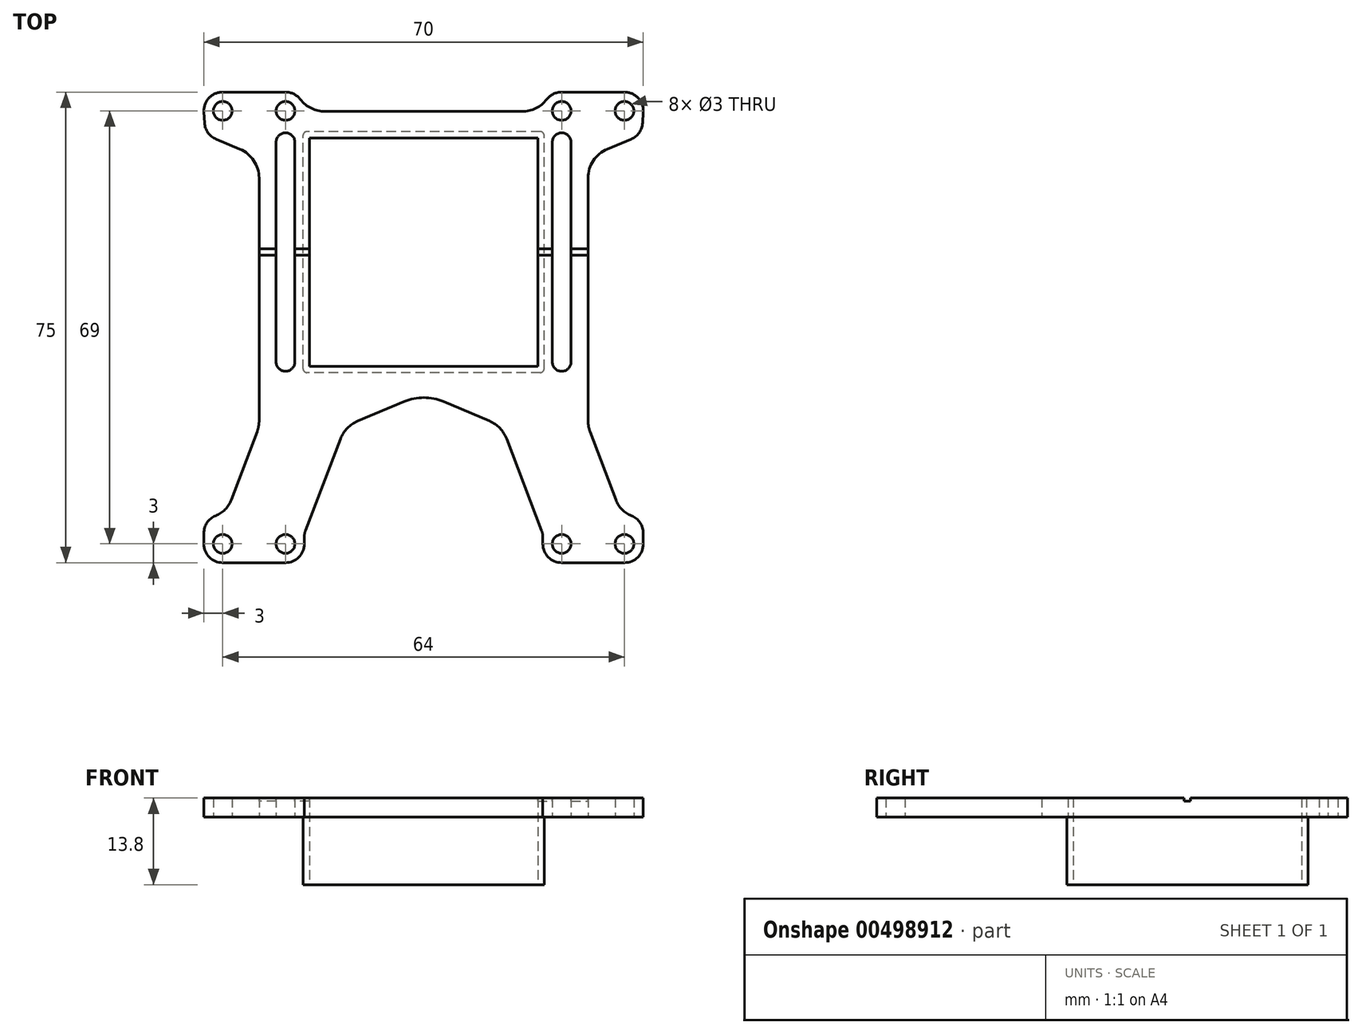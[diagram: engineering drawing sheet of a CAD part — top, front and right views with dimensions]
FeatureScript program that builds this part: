
annotation { "Feature Type Name" : "Feature", "Feature Type Description" : "" }
export const myFeature = defineFeature(function(context is Context, id is Id, definition is map)
    precondition{}
    {
        {
            var Q0;
            Q0=qCreatedBy(makeId("Top.planeOp"),FACE);
            var sketch = newSketch(context, id + "F0", { "sketchPlane" : qUnion([Q0])});
            skLineSegment(sketch, "E0.bottom", {"start": v(-1.83, 2.38) * mm, "end": v(1.83, 2.38) * mm, "construction": true});
            skLineSegment(sketch, "E0.top", {"start": v(-1.83, -2.37) * mm, "end": v(1.83, -2.37) * mm, "construction": true});
            skLineSegment(sketch, "E0.left", {"start": v(-1.83, 2.38) * mm, "end": v(-1.83, -2.37) * mm, "construction": true});
            skLineSegment(sketch, "E0.right", {"start": v(1.83, 2.38) * mm, "end": v(1.83, -2.37) * mm, "construction": true});
            skLineSegment(sketch, "E1.bottom", {"start": v(-1.28, 1.65) * mm, "end": v(1.32, 1.65) * mm, "construction": true});
            skLineSegment(sketch, "E1.top", {"start": v(-1.28, -0.31) * mm, "end": v(1.32, -0.31) * mm, "construction": true});
            skLineSegment(sketch, "E1.left", {"start": v(-1.28, 1.65) * mm, "end": v(-1.28, -0.31) * mm, "construction": true});
            skLineSegment(sketch, "E1.right", {"start": v(1.32, 1.65) * mm, "end": v(1.32, -0.31) * mm, "construction": true});
            skLineSegment(sketch, "E2", {"start": v(-1.28, 1.65) * mm, "end": v(1.32, -0.31) * mm, "construction": true});
            skLineSegment(sketch, "E3", {"start": v(1.32, 1.65) * mm, "end": v(-1.28, -0.31) * mm, "construction": true});
            skPoint(sketch, "E4", {"position": v(0.02, 0.67) * mm});
            skLineSegment(sketch, "E5.bottom", {"start": v(35, -49.5) * mm, "end": v(-35, -49.5) * mm, "construction": true});
            skLineSegment(sketch, "E5.top", {"start": v(35, 40.5) * mm, "end": v(-35, 40.5) * mm, "construction": true});
            skLineSegment(sketch, "E5.left", {"start": v(35, -49.5) * mm, "end": v(35, 40.5) * mm, "construction": true});
            skLineSegment(sketch, "E5.right", {"start": v(-35, -49.5) * mm, "end": v(-35, 40.5) * mm, "construction": true});
            skPoint(sketch, "E5.middle", {"position": v(0, 0) * mm});
            skLineSegment(sketch, "E6.bottom", {"start": v(18, -18) * mm, "end": v(-18, -18) * mm, "construction": true});
            skLineSegment(sketch, "E6.top", {"start": v(18, 18) * mm, "end": v(-18, 18) * mm, "construction": true});
            skLineSegment(sketch, "E6.left", {"start": v(18, -18) * mm, "end": v(18, 18) * mm, "construction": true});
            skLineSegment(sketch, "E6.right", {"start": v(-18, -18) * mm, "end": v(-18, 18) * mm, "construction": true});
            skPoint(sketch, "E7", {"position": v(-32, -46.5) * mm});
            skPoint(sketch, "E8", {"position": v(-22, -46.5) * mm});
            skPoint(sketch, "E9", {"position": v(22, -46.5) * mm});
            skPoint(sketch, "E10", {"position": v(32, -46.5) * mm});
            skPoint(sketch, "E11", {"position": v(32, 22.5) * mm});
            skPoint(sketch, "E12", {"position": v(22, 22.5) * mm});
            skPoint(sketch, "E12.positionSnap0", {"position": v(18, 0) * mm});
            skPoint(sketch, "E13", {"position": v(-22, 22.5) * mm});
            skPoint(sketch, "E14", {"position": v(-32, 22.5) * mm});
            skCircle(sketch, "E15", {"center": v(-32, 22.5) * mm, "radius": 1.25 * mm, "construction": true});
            skCircle(sketch, "E16", {"center": v(-22, 22.5) * mm, "radius": 1.25 * mm, "construction": true});
            skCircle(sketch, "E17", {"center": v(22, 22.5) * mm, "radius": 1.25 * mm, "construction": true});
            skCircle(sketch, "E18", {"center": v(32, 22.5) * mm, "radius": 1.25 * mm, "construction": true});
            skCircle(sketch, "E19", {"center": v(-32, -46.5) * mm, "radius": 1.25 * mm, "construction": true});
            skCircle(sketch, "E20", {"center": v(22, -46.5) * mm, "radius": 1.25 * mm, "construction": true});
            skCircle(sketch, "E21", {"center": v(32, -46.5) * mm, "radius": 1.25 * mm, "construction": true});
            skCircle(sketch, "E22", {"center": v(-22, -46.5) * mm, "radius": 1.25 * mm, "construction": true});
            skLineSegment(sketch, "E23.bottom", {"start": v(15, -15) * mm, "end": v(-15, -15) * mm, "construction": true});
            skLineSegment(sketch, "E23.top", {"start": v(15, 15) * mm, "end": v(-15, 15) * mm, "construction": true});
            skLineSegment(sketch, "E23.left", {"start": v(15, -15) * mm, "end": v(15, 15) * mm, "construction": true});
            skLineSegment(sketch, "E23.right", {"start": v(-15, -15) * mm, "end": v(-15, 15) * mm, "construction": true});
            skLineSegment(sketch, "E24.bottom", {"start": v(9.5, -9.5) * mm, "end": v(-9.5, -9.5) * mm, "construction": true});
            skLineSegment(sketch, "E24.top", {"start": v(9.5, 9.5) * mm, "end": v(-9.5, 9.5) * mm, "construction": true});
            skLineSegment(sketch, "E24.left", {"start": v(9.5, -9.5) * mm, "end": v(9.5, 9.5) * mm, "construction": true});
            skLineSegment(sketch, "E24.right", {"start": v(-9.5, -9.5) * mm, "end": v(-9.5, 9.5) * mm, "construction": true});
            skSolve(sketch);
        }
        {
            var Q0;
            Q0=qCreatedBy(makeId("Top.planeOp"),FACE);
            var sketch = newSketch(context, id + "F1", { "sketchPlane" : qUnion([Q0])});
            skLineSegment(sketch, "E25.bottom", {"start": v(18.2, -18.2) * mm, "end": v(-18.2, -18.2) * mm});
            skLineSegment(sketch, "E25.top", {"start": v(18.2, 18.2) * mm, "end": v(-18.2, 18.2) * mm});
            skLineSegment(sketch, "E25.left", {"start": v(18.2, -18.2) * mm, "end": v(18.2, 18.2) * mm});
            skLineSegment(sketch, "E25.right", {"start": v(-18.2, -18.2) * mm, "end": v(-18.2, 18.2) * mm});
            skPoint(sketch, "E25.middle", {"position": v(0, 0) * mm});
            skLineSegment(sketch, "E26.bottom", {"start": v(19.2, -19.2) * mm, "end": v(-19.2, -19.2) * mm});
            skLineSegment(sketch, "E26.top", {"start": v(19.2, 19.2) * mm, "end": v(-19.2, 19.2) * mm});
            skLineSegment(sketch, "E26.left", {"start": v(19.2, -19.2) * mm, "end": v(19.2, 19.2) * mm});
            skLineSegment(sketch, "E26.right", {"start": v(-19.2, -19.2) * mm, "end": v(-19.2, 19.2) * mm});
            skSolve(sketch);
        }
        {
            var Q0;
            Q0=makeQuery(id+"F1.imprint","IMPRINT",FACE,{"disambiguationData":[TD([[makeQuery(id+"F1.imprint","IMPRINT",EDGE,{"derivedFrom":sQuery(id+"F1.wireOp",EDGE,"E25.bottom")}),1.0]])]});
            extrude(context, id + "F2", {"entities" : qUnion([Q0]), "depth" : (4.8 + 7) * mm, "offsetDistance" : 25 * mm});
        }
        {
            var Q0;
            Q0=makeQuery(id+"F2.opExtrude","CAP_FACE",FACE,{"disambiguationData":[OSD([sQuery(id+"F1.wireOp",EDGE,"E25.bottom"),sQuery(id+"F1.wireOp",EDGE,"E25.top"),sQuery(id+"F1.wireOp",EDGE,"E25.left"),sQuery(id+"F1.wireOp",EDGE,"E25.right"),sQuery(id+"F1.wireOp",EDGE,"E26.bottom"),sQuery(id+"F1.wireOp",EDGE,"E26.top"),sQuery(id+"F1.wireOp",EDGE,"E26.left"),sQuery(id+"F1.wireOp",EDGE,"E26.right")])],"isStart":false});
            var sketch = newSketch(context, id + "F3", { "sketchPlane" : qUnion([Q0])});
            skPoint(sketch, "E27.0", {"position": v(-35, -49.5) * mm});
            skPoint(sketch, "E28.0", {"position": v(35, -49.5) * mm});
            skLineSegment(sketch, "E29", {"start": v(-35, 25.5) * mm, "end": v(35, 25.5) * mm, "construction": true});
            skLineSegment(sketch, "E30.bottom", {"start": v(-32, -49.5) * mm, "end": v(-22, -49.5) * mm});
            skLineSegment(sketch, "E30.left", {"start": v(-35, -46.5) * mm, "end": v(-35, -44.8) * mm});
            skLineSegment(sketch, "E30.right", {"start": v(-19, -46.5) * mm, "end": v(-19, -45.44) * mm});
            skLineSegment(sketch, "E31.bottom", {"start": v(32, -49.5) * mm, "end": v(22, -49.5) * mm});
            skLineSegment(sketch, "E31.left", {"start": v(35, -46.5) * mm, "end": v(35, -44.8) * mm});
            skLineSegment(sketch, "E31.right", {"start": v(19, -46.5) * mm, "end": v(19, -45.44) * mm});
            skPoint(sketch, "E32.0", {"position": v(-19.2, -19.2) * mm});
            skPoint(sketch, "E33.0", {"position": v(19.2, -19.2) * mm});
            skArc(sketch, "E34", {"start": v(-30.65, -39.5) * mm, "mid": v(-31.62, -41.02) * mm, "end": v(-33.12, -42.02) * mm});
            skLineSegment(sketch, "E35", {"start": v(-18.8, -44.37) * mm, "end": v(-13.23, -29.76) * mm});
            skArc(sketch, "E36.MirrorCS", {"start": v(30.65, -39.5) * mm, "mid": v(31.62, -41.02) * mm, "end": v(33.12, -42.02) * mm});
            skLineSegment(sketch, "E37.MirrorCS", {"start": v(18.8, -44.37) * mm, "end": v(13.23, -29.76) * mm});
            skPoint(sketch, "E38.orphan", {"position": v(19, -39.5) * mm});
            skPoint(sketch, "E39.orphan", {"position": v(-19, -39.5) * mm});
            skPoint(sketch, "E40.visualSharp", {"position": v(-35, -42.32) * mm});
            skArc(sketch, "E40.filletArc", {"start": v(-33.12, -42.02) * mm, "mid": v(-34.48, -43.12) * mm, "end": v(-35, -44.8) * mm});
            skPoint(sketch, "E41.visualSharp", {"position": v(35, -42.32) * mm});
            skArc(sketch, "E41.filletArc", {"start": v(35, -44.8) * mm, "mid": v(34.48, -43.12) * mm, "end": v(33.12, -42.02) * mm});
            skArc(sketch, "E42.filletArc", {"start": v(32, -49.5) * mm, "mid": v(34.12, -48.62) * mm, "end": v(35, -46.5) * mm});
            skPoint(sketch, "E43.visualSharp", {"position": v(19, -49.5) * mm});
            skArc(sketch, "E43.filletArc", {"start": v(19, -46.5) * mm, "mid": v(19.88, -48.62) * mm, "end": v(22, -49.5) * mm});
            skPoint(sketch, "E44.visualSharp", {"position": v(-19, -49.5) * mm});
            skArc(sketch, "E44.filletArc", {"start": v(-22, -49.5) * mm, "mid": v(-19.88, -48.62) * mm, "end": v(-19, -46.5) * mm});
            skArc(sketch, "E45.filletArc", {"start": v(-35, -46.5) * mm, "mid": v(-34.12, -48.62) * mm, "end": v(-32, -49.5) * mm});
            skPoint(sketch, "E46.visualSharp", {"position": v(-19, -44.89) * mm});
            skArc(sketch, "E46.filletArc", {"start": v(-18.8, -44.37) * mm, "mid": v(-18.95, -44.9) * mm, "end": v(-19, -45.44) * mm});
            skPoint(sketch, "E47.visualSharp", {"position": v(19, -44.89) * mm});
            skArc(sketch, "E47.filletArc", {"start": v(19, -45.44) * mm, "mid": v(18.95, -44.9) * mm, "end": v(18.8, -44.37) * mm});
            skPoint(sketch, "E48.0", {"position": v(-32, 22.5) * mm});
            skPoint(sketch, "E49.0", {"position": v(-22, 22.5) * mm});
            skPoint(sketch, "E50.0", {"position": v(22, 22.5) * mm});
            skPoint(sketch, "E51.0", {"position": v(32, 22.5) * mm});
            skLineSegment(sketch, "E52.bottom", {"start": v(-32, 25.5) * mm, "end": v(-22, 25.5) * mm});
            skLineSegment(sketch, "E52.left", {"start": v(-35, 22.32) * mm, "end": v(-34.9, 20.58) * mm});
            skArc(sketch, "E53.filletArc", {"start": v(-34.9, 20.58) * mm, "mid": v(-34.34, 19.02) * mm, "end": v(-33.05, 18) * mm});
            skArc(sketch, "E54.filletArc", {"start": v(-32, 25.5) * mm, "mid": v(-34.18, 24.56) * mm, "end": v(-35, 22.32) * mm});
            skArc(sketch, "E55.filletArc", {"start": v(-19.63, 24.33) * mm, "mid": v(-20.68, 25.19) * mm, "end": v(-22, 25.5) * mm});
            skLineSegment(sketch, "E56", {"start": v(-33.05, 18) * mm, "end": v(-29.27, 16.41) * mm});
            skLineSegment(sketch, "E57.MirrorCS", {"start": v(35, 22.32) * mm, "end": v(34.9, 20.58) * mm});
            skArc(sketch, "E58.MirrorCS", {"start": v(19.63, 24.33) * mm, "mid": v(20.68, 25.19) * mm, "end": v(22, 25.5) * mm});
            skArc(sketch, "E59.MirrorCS", {"start": v(34.9, 20.58) * mm, "mid": v(34.34, 19.02) * mm, "end": v(33.05, 18) * mm});
            skArc(sketch, "E60.MirrorCS", {"start": v(32, 25.5) * mm, "mid": v(34.18, 24.56) * mm, "end": v(35, 22.32) * mm});
            skLineSegment(sketch, "E61.MirrorCS", {"start": v(32, 25.5) * mm, "end": v(22, 25.5) * mm});
            skLineSegment(sketch, "E62.MirrorCS", {"start": v(33.05, 18) * mm, "end": v(29.27, 16.41) * mm});
            skLineSegment(sketch, "E63", {"start": v(-15.68, 22.4) * mm, "end": v(15.68, 22.4) * mm});
            skLineSegment(sketch, "E64", {"start": v(-26.2, -26.85) * mm, "end": v(-26.2, 11.8) * mm});
            skLineSegment(sketch, "E65", {"start": v(-32, 22.5) * mm, "end": v(-22, 22.5) * mm, "construction": true});
            skCircle(sketch, "E66", {"center": v(-32, 22.5) * mm, "radius": 1.5 * mm});
            skCircle(sketch, "E67", {"center": v(32, 22.5) * mm, "radius": 1.5 * mm});
            skCircle(sketch, "E68", {"center": v(-32, -46.5) * mm, "radius": 1.5 * mm});
            skCircle(sketch, "E69", {"center": v(-22, -46.5) * mm, "radius": 1.5 * mm});
            skCircle(sketch, "E70", {"center": v(22, -46.5) * mm, "radius": 1.5 * mm});
            skCircle(sketch, "E71", {"center": v(32, -46.5) * mm, "radius": 1.5 * mm});
            skCircle(sketch, "E72", {"center": v(-22, 22.5) * mm, "radius": 1.5 * mm});
            skCircle(sketch, "E73", {"center": v(22, 22.5) * mm, "radius": 1.5 * mm});
            skCircle(sketch, "E74.0", {"center": v(-22, 0) * mm, "radius": 1.5 * mm, "construction": true});
            skCircle(sketch, "E75.0", {"center": v(-22, 10) * mm, "radius": 1.5 * mm, "construction": true});
            skCircle(sketch, "E76.0", {"center": v(-22, -10) * mm, "radius": 1.5 * mm, "construction": true});
            skArc(sketch, "E77.0.1.0", {"start": v(-23.5, -17.5) * mm, "mid": v(-22, -19) * mm, "end": v(-20.5, -17.5) * mm});
            skLineSegment(sketch, "E77.direction1", {"start": v(-22, -10) * mm, "end": v(3, -10) * mm, "construction": true});
            skLineSegment(sketch, "E77.direction2", {"start": v(-22, -10) * mm, "end": v(-22, -17.5) * mm, "construction": true});
            skArc(sketch, "E78.0.1.0", {"start": v(-20.5, 17.5) * mm, "mid": v(-22, 19) * mm, "end": v(-23.5, 17.5) * mm});
            skLineSegment(sketch, "E78.direction1", {"start": v(-22, 10) * mm, "end": v(3, 10) * mm, "construction": true});
            skLineSegment(sketch, "E78.direction2", {"start": v(-22, 10) * mm, "end": v(-22, 17.5) * mm, "construction": true});
            skLineSegment(sketch, "E79", {"start": v(-20.5, 17.5) * mm, "end": v(-20.5, -17.5) * mm});
            skLineSegment(sketch, "E80", {"start": v(-23.5, 17.5) * mm, "end": v(-23.5, -17.5) * mm});
            skArc(sketch, "E81.trimOffspring", {"start": v(-21.84, -16) * mm, "mid": v(-21.92, -16) * mm, "end": v(-22, -16) * mm});
            skLineSegment(sketch, "E82", {"start": v(-10.5, -26.94) * mm, "end": v(-3.06, -23.82) * mm});
            skLineSegment(sketch, "E83", {"start": v(3.15, -23.82) * mm, "end": v(10.5, -26.93) * mm});
            skPoint(sketch, "E84.orphan", {"position": v(-10.37, -22.5) * mm});
            skPoint(sketch, "E85.end.orphan", {"position": v(10.47, -22.53) * mm});
            skPoint(sketch, "E86.visualSharp", {"position": v(0.05, -22.51) * mm});
            skArc(sketch, "E86.filletArc", {"start": v(3.15, -23.82) * mm, "mid": v(0.05, -23.2) * mm, "end": v(-3.06, -23.82) * mm});
            skPoint(sketch, "E87.orphan", {"position": v(-26.2, 16.8) * mm});
            skPoint(sketch, "E88.trimOffspring.end.orphan", {"position": v(-19.2, 12.2) * mm});
            skLineSegment(sketch, "E89.trimOffspring", {"start": v(-26.52, -28.62) * mm, "end": v(-30.65, -39.5) * mm});
            skPoint(sketch, "E90.start.orphan", {"position": v(-19.2, -9.2) * mm});
            skPoint(sketch, "E91.trimOffspring.end.orphan", {"position": v(-9.2, -19.2) * mm});
            skPoint(sketch, "E92.orphan", {"position": v(9.2, -19.2) * mm});
            skLineSegment(sketch, "E93.MirrorCS", {"start": v(26.2, -26.85) * mm, "end": v(26.2, 11.8) * mm});
            skCircle(sketch, "E94.MirrorC", {"center": v(22, 10) * mm, "radius": 1.5 * mm, "construction": true});
            skLineSegment(sketch, "E95.MirrorCS", {"start": v(23.5, 17.5) * mm, "end": v(23.5, -17.5) * mm});
            skLineSegment(sketch, "E96.MirrorCS", {"start": v(22, -10) * mm, "end": v(22, -17.5) * mm, "construction": true});
            skLineSegment(sketch, "E97.MirrorCS", {"start": v(22, 10) * mm, "end": v(22, 17.5) * mm, "construction": true});
            skCircle(sketch, "E98.MirrorC", {"center": v(22, -10) * mm, "radius": 1.5 * mm, "construction": true});
            skArc(sketch, "E99.MirrorCS", {"start": v(20.5, 17.5) * mm, "mid": v(22, 19) * mm, "end": v(23.5, 17.5) * mm});
            skArc(sketch, "E100.MirrorCS", {"start": v(23.5, -17.5) * mm, "mid": v(22, -19) * mm, "end": v(20.5, -17.5) * mm});
            skLineSegment(sketch, "E101.MirrorCS", {"start": v(20.5, 17.5) * mm, "end": v(20.5, -17.5) * mm});
            skCircle(sketch, "E102.MirrorC", {"center": v(22, 0) * mm, "radius": 1.5 * mm, "construction": true});
            skLineSegment(sketch, "E103.trimOffspring", {"start": v(26.52, -28.62) * mm, "end": v(30.65, -39.5) * mm});
            skPoint(sketch, "E104.MirrorCS.end.orphan", {"position": v(22, -16) * mm});
            skPoint(sketch, "E104.MirrorCS.start.orphan", {"position": v(21.84, -16) * mm});
            skPoint(sketch, "E105.end.orphan", {"position": v(19.2, 12.2) * mm});
            skPoint(sketch, "E105.start.orphan", {"position": v(19.2, -9.2) * mm});
            skPoint(sketch, "E106.MirrorCS.end.orphan", {"position": v(19, 19.2) * mm});
            skPoint(sketch, "E107.MirrorCS.end.orphan", {"position": v(19, 21.46) * mm});
            skPoint(sketch, "E108.end.orphan", {"position": v(-19, 19.2) * mm});
            skPoint(sketch, "E52.right.end.orphan", {"position": v(-19, 21.46) * mm});
            skPoint(sketch, "E109.visualSharp", {"position": v(-26.2, -27.76) * mm});
            skArc(sketch, "E109.filletArc", {"start": v(-26.52, -28.62) * mm, "mid": v(-26.28, -27.75) * mm, "end": v(-26.2, -26.85) * mm});
            skPoint(sketch, "E110.visualSharp", {"position": v(26.2, -27.76) * mm});
            skArc(sketch, "E110.filletArc", {"start": v(26.2, -26.85) * mm, "mid": v(26.28, -27.75) * mm, "end": v(26.52, -28.62) * mm});
            skPoint(sketch, "E111.visualSharp", {"position": v(-12.47, -27.76) * mm});
            skArc(sketch, "E111.filletArc", {"start": v(-10.5, -26.94) * mm, "mid": v(-12.15, -28.07) * mm, "end": v(-13.23, -29.76) * mm});
            skPoint(sketch, "E112.visualSharp", {"position": v(12.47, -27.76) * mm});
            skArc(sketch, "E112.filletArc", {"start": v(13.23, -29.76) * mm, "mid": v(12.15, -28.07) * mm, "end": v(10.5, -26.93) * mm});
            skPoint(sketch, "E113.visualSharp", {"position": v(-19, 22.4) * mm});
            skArc(sketch, "E113.filletArc", {"start": v(-19.63, 24.33) * mm, "mid": v(-17.88, 22.9) * mm, "end": v(-15.68, 22.4) * mm});
            skPoint(sketch, "E114.visualSharp", {"position": v(19, 22.4) * mm});
            skArc(sketch, "E114.filletArc", {"start": v(15.68, 22.4) * mm, "mid": v(17.88, 22.9) * mm, "end": v(19.63, 24.33) * mm});
            skPoint(sketch, "E115.visualSharp", {"position": v(26.2, 15.13) * mm});
            skArc(sketch, "E115.filletArc", {"start": v(29.27, 16.41) * mm, "mid": v(27.04, 14.57) * mm, "end": v(26.2, 11.8) * mm});
            skPoint(sketch, "E116.visualSharp", {"position": v(-26.2, 15.13) * mm});
            skArc(sketch, "E116.filletArc", {"start": v(-26.2, 11.8) * mm, "mid": v(-27.04, 14.57) * mm, "end": v(-29.27, 16.41) * mm});
            skPoint(sketch, "E117.0", {"position": v(0, 0) * mm});
            skSolve(sketch);
        }
        {
            var Q0;
            Q0=makeQuery(id+"F3.imprint","IMPRINT",FACE,{"disambiguationData":[TD([[makeQuery(id+"F3.imprint","IMPRINT",EDGE,{"derivedFrom":sQuery(id+"F3.wireOp",EDGE,"E30.bottom")}),1.0]])]});
            var Q1;
            Q1=makeQuery(id+"F3.imprint","IMPRINT",FACE,{"disambiguationData":[TD([[makeQuery(id+"F3.imprint","IMPRINT",EDGE,{"derivedFrom":makeQuery(id+"F2.opExtrude","CAP_EDGE",EDGE,{"disambiguationData":[OSD([sQuery(id+"F1.wireOp",EDGE,"E25.bottom")])],"isStart":false})}),1.0]])]});
            extrude(context, id + "F4", {"entities" : qUnion([Q0, Q1]), "operationType" : NewBodyOperationType.ADD, "depth" : 2 * mm, "hasSecondDirection" : true, "secondDirectionOppositeDirection" : true, "secondDirectionDepth" : 1 * mm, "offsetDistance" : 25 * mm});
        }
        {
            var Q0;
            Q0=makeQuery(id+"F2.opExtrude","SWEPT_EDGE",EDGE,{"disambiguationData":[OSD([sQuery(id+"F1.wireOp",EDGE,"E26.bottom"),sQuery(id+"F1.wireOp",EDGE,"E26.right")])]});
            var Q1;
            Q1=makeQuery(id+"F2.opExtrude","SWEPT_EDGE",EDGE,{"disambiguationData":[OSD([sQuery(id+"F1.wireOp",EDGE,"E26.bottom"),sQuery(id+"F1.wireOp",EDGE,"E26.left")])]});
            var Q2;
            Q2=makeQuery(id+"F2.opExtrude","SWEPT_EDGE",EDGE,{"disambiguationData":[OSD([sQuery(id+"F1.wireOp",EDGE,"E26.top"),sQuery(id+"F1.wireOp",EDGE,"E26.left")])]});
            var Q3;
            Q3=makeQuery(id+"F2.opExtrude","SWEPT_EDGE",EDGE,{"disambiguationData":[OSD([sQuery(id+"F1.wireOp",EDGE,"E26.top"),sQuery(id+"F1.wireOp",EDGE,"E26.right")])]});
            fillet(context, id + "F5", {"entities" : qUnion([Q0, Q1, Q2, Q3]), "radius" : 0.6 * mm, "tangentPropagation" : true, "allowEdgeOverflow" : false});
        }
        {
            var Q0;
            Q0=makeQuery(id+"F4.opExtrude","CAP_FACE",FACE,{"disambiguationData":[OSD([sQuery(id+"F1.wireOp",EDGE,"E25.bottom"),sQuery(id+"F1.wireOp",EDGE,"E25.top"),sQuery(id+"F1.wireOp",EDGE,"E25.left"),sQuery(id+"F1.wireOp",EDGE,"E25.right"),sQuery(id+"F3.wireOp",EDGE,"E30.bottom"),sQuery(id+"F3.wireOp",EDGE,"E30.left"),sQuery(id+"F3.wireOp",EDGE,"E30.right"),sQuery(id+"F3.wireOp",EDGE,"E31.bottom"),sQuery(id+"F3.wireOp",EDGE,"E31.left"),sQuery(id+"F3.wireOp",EDGE,"E31.right"),sQuery(id+"F3.wireOp",EDGE,"E34"),sQuery(id+"F3.wireOp",EDGE,"E35"),sQuery(id+"F3.wireOp",EDGE,"E36.MirrorCS"),sQuery(id+"F3.wireOp",EDGE,"E37.MirrorCS"),sQuery(id+"F3.wireOp",EDGE,"E40.filletArc"),sQuery(id+"F3.wireOp",EDGE,"E41.filletArc"),sQuery(id+"F3.wireOp",EDGE,"E42.filletArc"),sQuery(id+"F3.wireOp",EDGE,"E43.filletArc"),sQuery(id+"F3.wireOp",EDGE,"E44.filletArc"),sQuery(id+"F3.wireOp",EDGE,"E45.filletArc"),sQuery(id+"F3.wireOp",EDGE,"E46.filletArc"),sQuery(id+"F3.wireOp",EDGE,"E47.filletArc"),sQuery(id+"F3.wireOp",EDGE,"E52.bottom"),sQuery(id+"F3.wireOp",EDGE,"E52.left"),sQuery(id+"F3.wireOp",EDGE,"E53.filletArc"),sQuery(id+"F3.wireOp",EDGE,"E54.filletArc"),sQuery(id+"F3.wireOp",EDGE,"E55.filletArc"),sQuery(id+"F3.wireOp",EDGE,"E56"),sQuery(id+"F3.wireOp",EDGE,"E57.MirrorCS"),sQuery(id+"F3.wireOp",EDGE,"E58.MirrorCS"),sQuery(id+"F3.wireOp",EDGE,"E59.MirrorCS"),sQuery(id+"F3.wireOp",EDGE,"E60.MirrorCS"),sQuery(id+"F3.wireOp",EDGE,"E61.MirrorCS"),sQuery(id+"F3.wireOp",EDGE,"E62.MirrorCS"),sQuery(id+"F3.wireOp",EDGE,"E63"),sQuery(id+"F3.wireOp",EDGE,"E64"),sQuery(id+"F3.wireOp",EDGE,"E66"),sQuery(id+"F3.wireOp",EDGE,"E67"),sQuery(id+"F3.wireOp",EDGE,"E68"),sQuery(id+"F3.wireOp",EDGE,"E69"),sQuery(id+"F3.wireOp",EDGE,"E70"),sQuery(id+"F3.wireOp",EDGE,"E71"),sQuery(id+"F3.wireOp",EDGE,"E72"),sQuery(id+"F3.wireOp",EDGE,"E73"),sQuery(id+"F3.wireOp",EDGE,"E77.0.1.0"),sQuery(id+"F3.wireOp",EDGE,"E78.0.1.0"),sQuery(id+"F3.wireOp",EDGE,"E79"),sQuery(id+"F3.wireOp",EDGE,"E80"),sQuery(id+"F3.wireOp",EDGE,"E82"),sQuery(id+"F3.wireOp",EDGE,"E83"),sQuery(id+"F3.wireOp",EDGE,"E86.filletArc"),sQuery(id+"F3.wireOp",EDGE,"E89.trimOffspring"),sQuery(id+"F3.wireOp",EDGE,"E93.MirrorCS"),sQuery(id+"F3.wireOp",EDGE,"E95.MirrorCS"),sQuery(id+"F3.wireOp",EDGE,"E99.MirrorCS"),sQuery(id+"F3.wireOp",EDGE,"E100.MirrorCS"),sQuery(id+"F3.wireOp",EDGE,"E101.MirrorCS"),sQuery(id+"F3.wireOp",EDGE,"E103.trimOffspring"),sQuery(id+"F3.wireOp",EDGE,"E109.filletArc"),sQuery(id+"F3.wireOp",EDGE,"E110.filletArc"),sQuery(id+"F3.wireOp",EDGE,"E111.filletArc"),sQuery(id+"F3.wireOp",EDGE,"E112.filletArc"),sQuery(id+"F3.wireOp",EDGE,"E113.filletArc"),sQuery(id+"F3.wireOp",EDGE,"E114.filletArc"),sQuery(id+"F3.wireOp",EDGE,"E115.filletArc"),sQuery(id+"F3.wireOp",EDGE,"E116.filletArc")])],"isStart":false});
            var sketch = newSketch(context, id + "F6", { "sketchPlane" : qUnion([Q0])});
            skLineSegment(sketch, "E118", {"start": v(0, 0) * mm, "end": v(-33.87, 0) * mm, "construction": true});
            skLineSegment(sketch, "E119.bottom", {"start": v(-18.2, 0.5) * mm, "end": v(-26.2, 0.5) * mm});
            skLineSegment(sketch, "E119.top", {"start": v(-18.2, -0.5) * mm, "end": v(-26.2, -0.5) * mm});
            skLineSegment(sketch, "E119.left", {"start": v(-18.2, 0.5) * mm, "end": v(-18.2, -0.5) * mm});
            skLineSegment(sketch, "E119.right", {"start": v(-26.2, 0.5) * mm, "end": v(-26.2, -0.5) * mm});
            skLineSegment(sketch, "E120.MirrorCS", {"start": v(18.2, 0.5) * mm, "end": v(18.2, -0.5) * mm});
            skLineSegment(sketch, "E121.MirrorCS", {"start": v(26.2, 0.5) * mm, "end": v(26.2, -0.5) * mm});
            skLineSegment(sketch, "E122.MirrorCS", {"start": v(18.2, -0.5) * mm, "end": v(26.2, -0.5) * mm});
            skLineSegment(sketch, "E123.MirrorCS", {"start": v(18.2, 0.5) * mm, "end": v(26.2, 0.5) * mm});
            skSolve(sketch);
        }
        {
            var Q0;
            {var subQ0=sQuery(id+"F6.wireOp",EDGE,"E119.right");Q0=makeQuery(id+"F6.imprint","IMPRINT",FACE,{"disambiguationData":[TD([[makeQuery(id+"F6.imprint","IMPRINT",EDGE,{"derivedFrom":subQ0}),-1.0]])]});}
            var Q1;
            {var subQ0=sQuery(id+"F6.wireOp",EDGE,"E119.left");Q1=makeQuery(id+"F6.imprint","IMPRINT",FACE,{"disambiguationData":[TD([[makeQuery(id+"F6.imprint","IMPRINT",EDGE,{"derivedFrom":subQ0}),1.0]])]});}
            var Q2;
            {var subQ0=sQuery(id+"F6.wireOp",EDGE,"E120.MirrorCS");Q2=makeQuery(id+"F6.imprint","IMPRINT",FACE,{"disambiguationData":[TD([[makeQuery(id+"F6.imprint","IMPRINT",EDGE,{"derivedFrom":subQ0}),-1.0]])]});}
            var Q3;
            {var subQ0=sQuery(id+"F6.wireOp",EDGE,"E121.MirrorCS");Q3=makeQuery(id+"F6.imprint","IMPRINT",FACE,{"disambiguationData":[TD([[makeQuery(id+"F6.imprint","IMPRINT",EDGE,{"derivedFrom":subQ0}),1.0]])]});}
            extrude(context, id + "F7", {"entities" : qUnion([Q0, Q1, Q2, Q3]), "operationType" : NewBodyOperationType.REMOVE, "oppositeDirection" : true, "depth" : 0.5 * mm});
        }
    });
